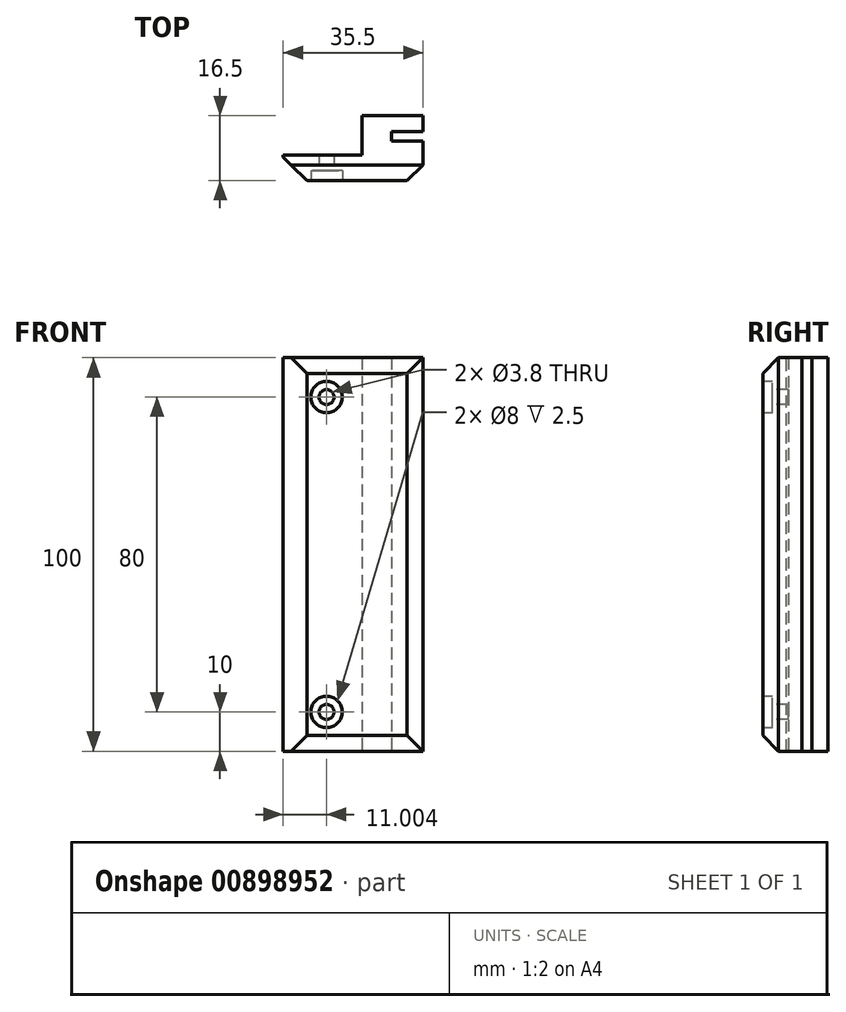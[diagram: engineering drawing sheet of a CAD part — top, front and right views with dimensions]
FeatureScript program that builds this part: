
annotation { "Feature Type Name" : "Feature", "Feature Type Description" : "" }
export const myFeature = defineFeature(function(context is Context, id is Id, definition is map)
    precondition{}
    {
        {
            var Q0;
            Q0=qCreatedBy(makeId("Top.planeOp"),FACE);
            var sketch = newSketch(context, id + "F0", { "sketchPlane" : qUnion([Q0])});
            skLineSegment(sketch, "E0", {"start": v(-34.07, 8.3) * mm, "end": v(-14.07, 8.3) * mm});
            skLineSegment(sketch, "E1", {"start": v(-14.07, 8.3) * mm, "end": v(-14.07, 18.3) * mm});
            skLineSegment(sketch, "E2", {"start": v(-14.07, 18.3) * mm, "end": v(1.43, 18.3) * mm});
            skLineSegment(sketch, "E3", {"start": v(1.43, 18.3) * mm, "end": v(1.43, 14.3) * mm});
            skLineSegment(sketch, "E4", {"start": v(1.43, 14.3) * mm, "end": v(-6.57, 14.3) * mm});
            skLineSegment(sketch, "E5", {"start": v(-6.57, 14.3) * mm, "end": v(-6.57, 11.8) * mm});
            skLineSegment(sketch, "E6", {"start": v(-6.57, 11.8) * mm, "end": v(1.43, 11.8) * mm});
            skLineSegment(sketch, "E7", {"start": v(1.43, 11.8) * mm, "end": v(1.43, 1.8) * mm});
            skLineSegment(sketch, "E8", {"start": v(1.43, 1.8) * mm, "end": v(-34.07, 1.8) * mm});
            skLineSegment(sketch, "E9", {"start": v(-34.07, 1.8) * mm, "end": v(-34.07, 8.3) * mm});
            skSolve(sketch);
        }
        {
            var Q0;
            Q0 = qSketchRegion(id + "F0", true);
            extrude(context, id + "F1", {"entities" : qUnion([Q0]), "depth" : 100 * mm, "offsetDistance" : 25 * mm});
        }
        {
            var Q0;
            Q0=makeQuery(id+"F1.opExtrude","CAP_EDGE",EDGE,{"disambiguationData":[OSD([sQuery(id+"F0.wireOp",EDGE,"E8")])],"isStart":false});
            var Q1;
            Q1=makeQuery(id+"F1.opExtrude","CAP_EDGE",EDGE,{"disambiguationData":[OSD([sQuery(id+"F0.wireOp",EDGE,"E8")])],"isStart":true});
            var Q2;
            Q2=makeQuery(id+"F1.opExtrude","SWEPT_EDGE",EDGE,{"disambiguationData":[OSD([sQuery(id+"F0.wireOp",EDGE,"E7"),sQuery(id+"F0.wireOp",EDGE,"E8")])]});
            chamfer(context, id + "F2", {"entities" : qUnion([Q0, Q1, Q2]), "width" : 4 * mm, "tangentPropagation" : true});
        }
        {
            var Q0;
            Q0=makeQuery(id+"F1.opExtrude","SWEPT_EDGE",EDGE,{"disambiguationData":[OSD([sQuery(id+"F0.wireOp",EDGE,"E8"),sQuery(id+"F0.wireOp",EDGE,"E9")])]});
            chamfer(context, id + "F3", {"entities" : qUnion([Q0]), "width" : 6 * mm, "tangentPropagation" : true});
        }
        {
            var Q0;
            Q0=makeQuery(id+"F1.opExtrude","SWEPT_FACE",FACE,{"disambiguationData":[OSD([sQuery(id+"F0.wireOp",EDGE,"E8")])]});
            var sketch = newSketch(context, id + "F4", { "sketchPlane" : qUnion([Q0])});
            skCircle(sketch, "E10", {"center": v(-23.07, 90) * mm, "radius": 1.9 * mm});
            skCircle(sketch, "E11", {"center": v(-23.07, 10) * mm, "radius": 1.9 * mm});
            skSolve(sketch);
        }
        {
            var Q0;
            Q0 = qSketchRegion(id + "F4", true);
            extrude(context, id + "F5", {"entities" : qUnion([Q0]), "operationType" : NewBodyOperationType.REMOVE, "oppositeDirection" : true, "depth" : 8 * mm, "offsetDistance" : 25 * mm});
        }
        {
            var Q0;
            Q0=makeQuery(id+"F1.opExtrude","SWEPT_FACE",FACE,{"disambiguationData":[OSD([sQuery(id+"F0.wireOp",EDGE,"E8")])]});
            var sketch = newSketch(context, id + "F6", { "sketchPlane" : qUnion([Q0])});
            skCircle(sketch, "E12", {"center": v(-23.07, 90) * mm, "radius": 4 * mm});
            skCircle(sketch, "E13", {"center": v(-23.07, 10) * mm, "radius": 4 * mm});
            skSolve(sketch);
        }
        {
            var Q0;
            Q0 = qSketchRegion(id + "F6", true);
            extrude(context, id + "F7", {"entities" : qUnion([Q0]), "operationType" : NewBodyOperationType.REMOVE, "oppositeDirection" : true, "depth" : 2.5 * mm, "offsetDistance" : 25 * mm});
        }
    });
